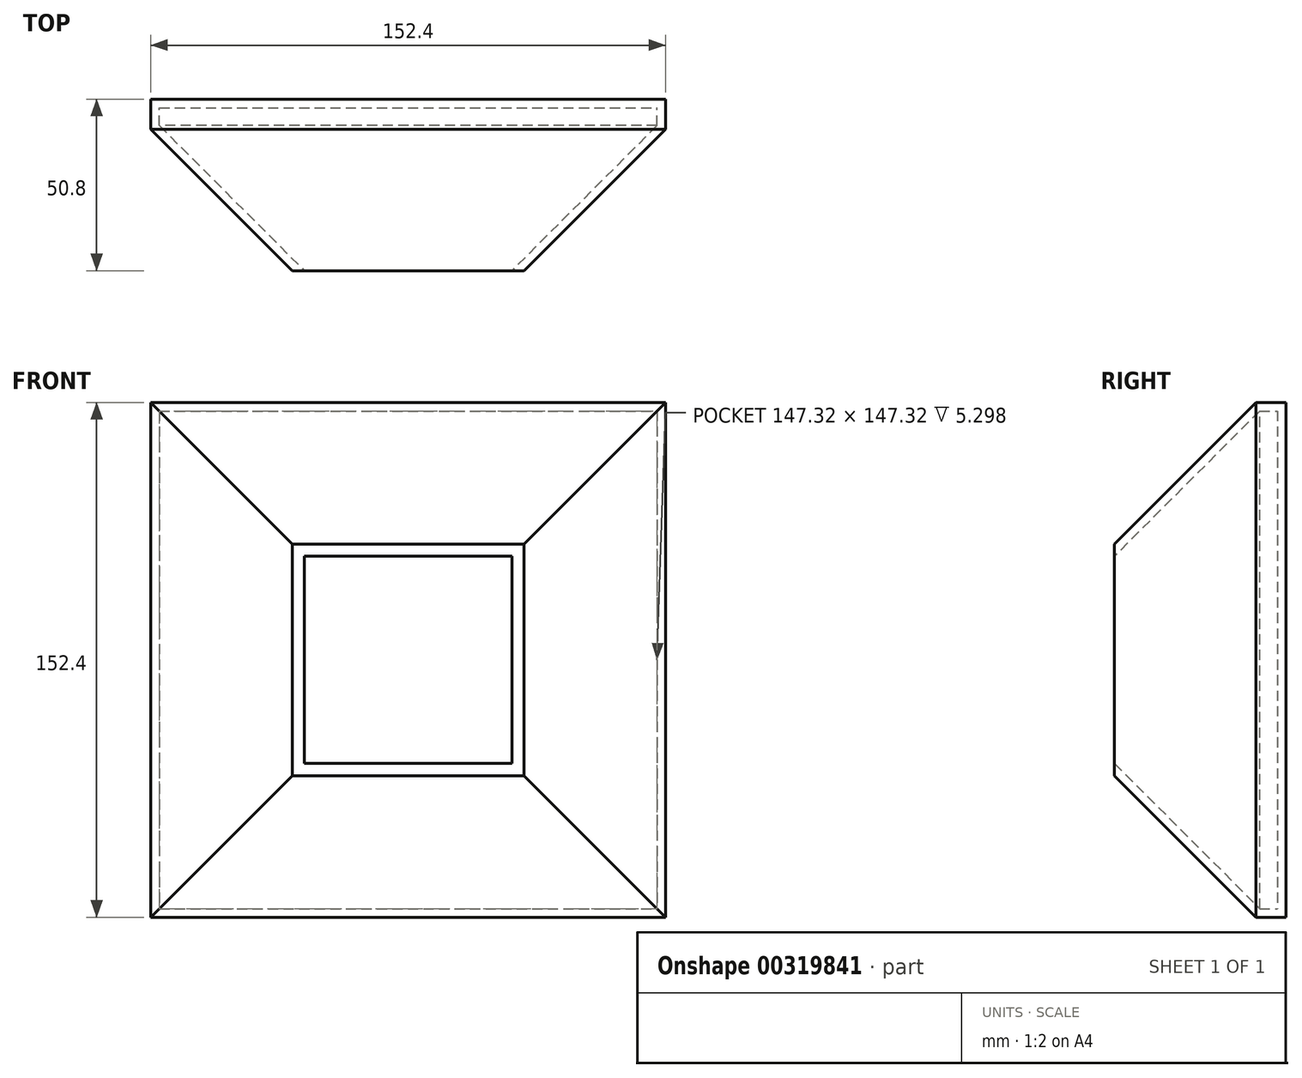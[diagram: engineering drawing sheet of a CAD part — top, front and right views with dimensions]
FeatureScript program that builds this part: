
annotation { "Feature Type Name" : "Feature", "Feature Type Description" : "" }
export const myFeature = defineFeature(function(context is Context, id is Id, definition is map)
    precondition{}
    {
        {
            var Q0;
            Q0=qCreatedBy(makeId("Front.planeOp"),FACE);
            var sketch = newSketch(context, id + "F0", { "sketchPlane" : qUnion([Q0])});
            skLineSegment(sketch, "E0.bottom", {"start": v(-76.2, 76.32) * mm, "end": v(76.2, 76.32) * mm});
            skLineSegment(sketch, "E0.top", {"start": v(-76.2, -76.08) * mm, "end": v(76.2, -76.08) * mm});
            skLineSegment(sketch, "E0.left", {"start": v(-76.2, 76.32) * mm, "end": v(-76.2, -76.08) * mm});
            skLineSegment(sketch, "E0.right", {"start": v(76.2, 76.32) * mm, "end": v(76.2, -76.08) * mm});
            skSolve(sketch);
        }
        {
            var Q0;
            Q0 = qSketchRegion(id + "F0", true);
            extrude(context, id + "F1", {"entities" : qUnion([Q0]), "depth" : 50.8 * mm});
        }
        {
            var Q0;
            Q0=makeQuery(id+"F1.opExtrude","CAP_FACE",FACE,{"disambiguationData":[OSD([sQuery(id+"F0.wireOp",EDGE,"E0.bottom"),sQuery(id+"F0.wireOp",EDGE,"E0.top"),sQuery(id+"F0.wireOp",EDGE,"E0.left"),sQuery(id+"F0.wireOp",EDGE,"E0.right")])],"isStart":false});
            chamfer(context, id + "F2", {"entities" : qUnion([Q0]), "width" : 41.9 * mm, "tangentPropagation" : true});
        }
        {
            var Q0;
            Q0=makeQuery(id+"F1.opExtrude","CAP_FACE",FACE,{"disambiguationData":[OSD([sQuery(id+"F0.wireOp",EDGE,"E0.bottom"),sQuery(id+"F0.wireOp",EDGE,"E0.top"),sQuery(id+"F0.wireOp",EDGE,"E0.left"),sQuery(id+"F0.wireOp",EDGE,"E0.right")])],"isStart":false});
            shell(context, id + "F3", {"entities" : qUnion([Q0]), "thickness" : 2.54 * mm});
        }
    });
